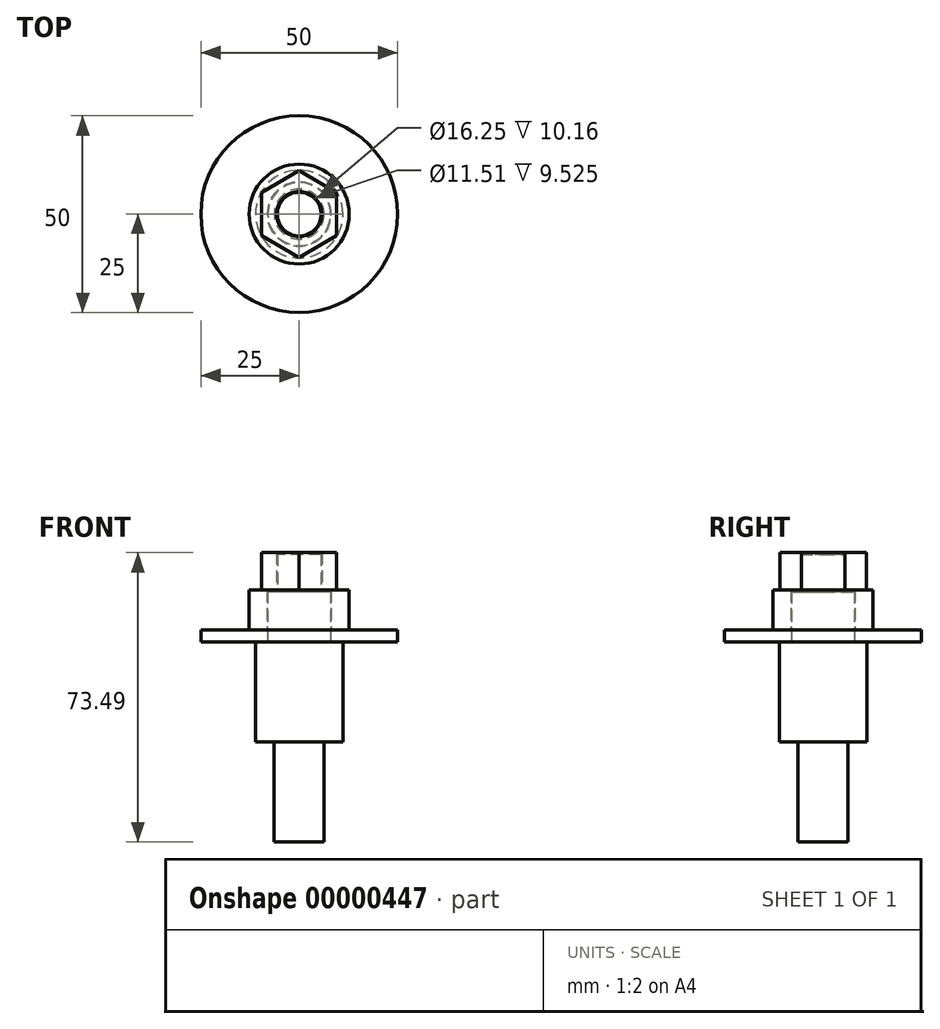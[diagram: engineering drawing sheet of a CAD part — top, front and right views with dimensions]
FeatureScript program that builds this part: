
annotation { "Feature Type Name" : "Feature", "Feature Type Description" : "" }
export const myFeature = defineFeature(function(context is Context, id is Id, definition is map)
    precondition{}
    {
        {
            var Q0;
            Q0=qCreatedBy(makeId("Top.planeOp"),FACE);
            var sketch = newSketch(context, id + "F0", { "sketchPlane" : qUnion([Q0])});
            skCircle(sketch, "E0", {"center": v(0, 0) * mm, "radius": 6.35 * mm});
            skSolve(sketch);
        }
        {
            var Q0;
            Q0 = qSketchRegion(id + "F0", true);
            extrude(context, id + "F1", {"entities" : qUnion([Q0]), "depth" : 25.4 * mm, "offsetDistance" : 25.4 * mm});
        }
        {
            var Q0;
            Q0=makeQuery(id+"F1.opExtrude","CAP_FACE",FACE,{"disambiguationData":[OSD([sQuery(id+"F0.wireOp",EDGE,"E0")])],"isStart":false});
            var sketch = newSketch(context, id + "F2", { "sketchPlane" : qUnion([Q0])});
            skCircle(sketch, "E1", {"center": v(0, 0) * mm, "radius": 11.11 * mm});
            skSolve(sketch);
        }
        {
            var Q0;
            Q0 = qSketchRegion(id + "F2", true);
            extrude(context, id + "F3", {"entities" : qUnion([Q0]), "operationType" : NewBodyOperationType.ADD, "depth" : 25.4 * mm, "offsetDistance" : 25.4 * mm});
        }
        {
            var Q0;
            Q0=makeQuery(id+"F3.opExtrude","CAP_FACE",FACE,{"disambiguationData":[OSD([sQuery(id+"F2.wireOp",EDGE,"E1")])],"isStart":false});
            var sketch = newSketch(context, id + "F4", { "sketchPlane" : qUnion([Q0])});
            skCircle(sketch, "E2", {"center": v(0, 0) * mm, "radius": 8 * mm});
            skSolve(sketch);
        }
        {
            var Q0;
            Q0 = qSketchRegion(id + "F4", true);
            extrude(context, id + "F5", {"entities" : qUnion([Q0]), "operationType" : NewBodyOperationType.ADD, "depth" : 12.7 * mm, "offsetDistance" : 25.4 * mm});
        }
        {
            var Q0;
            Q0=makeQuery(id+"F5.opExtrude","CAP_FACE",FACE,{"disambiguationData":[OSD([sQuery(id+"F4.wireOp",EDGE,"E2")])],"isStart":false});
            var sketch = newSketch(context, id + "F6", { "sketchPlane" : qUnion([Q0])});
            skCircle(sketch, "E3", {"center": v(0, 0) * mm, "radius": 5.55 * mm});
            skSolve(sketch);
        }
        {
            var Q0;
            Q0 = qSketchRegion(id + "F6", true);
            extrude(context, id + "F7", {"entities" : qUnion([Q0]), "operationType" : NewBodyOperationType.ADD, "depth" : 9.52 * mm, "offsetDistance" : 25.4 * mm});
        }
        {
            var Q0;
            Q0=makeQuery(id+"F3.opExtrude","CAP_FACE",FACE,{"disambiguationData":[OSD([sQuery(id+"F2.wireOp",EDGE,"E1")])],"isStart":false});
            var sketch = newSketch(context, id + "F8", { "sketchPlane" : qUnion([Q0])});
            skCircle(sketch, "E4", {"center": v(0, 0) * mm, "radius": 25 * mm});
            skSolve(sketch);
        }
        {
            var Q0;
            Q0 = qSketchRegion(id + "F8", true);
            extrude(context, id + "F9", {"entities" : qUnion([Q0]), "depth" : 3 * mm, "offsetDistance" : 25.4 * mm});
        }
        {
            var Q0;
            Q0=makeQuery(id+"F9.opExtrude","CAP_FACE",FACE,{"disambiguationData":[OSD([sQuery(id+"F8.wireOp",EDGE,"E4")])],"isStart":false});
            var sketch = newSketch(context, id + "F10", { "sketchPlane" : qUnion([Q0])});
            skCircle(sketch, "E5", {"center": v(0, 0) * mm, "radius": 12.7 * mm});
            skCircle(sketch, "E6", {"center": v(0, 0) * mm, "radius": 8.12 * mm});
            skSolve(sketch);
        }
        {
            var Q0;
            Q0 = qSketchRegion(id + "F10", true);
            extrude(context, id + "F11", {"entities" : qUnion([Q0]), "depth" : 10.16 * mm, "offsetDistance" : 25.4 * mm});
        }
        {
            var Q0;
            Q0=makeQuery(id+"F11.opExtrude","CAP_FACE",FACE,{"disambiguationData":[OSD([sQuery(id+"F10.wireOp",EDGE,"E5"),sQuery(id+"F10.wireOp",EDGE,"E6")])],"isStart":false});
            var sketch = newSketch(context, id + "F12", { "sketchPlane" : qUnion([Q0])});
            skCircle(sketch, "E7", {"center": v(0, 0) * mm, "radius": 5.75 * mm});
            skCircle(sketch, "E8.cCircle", {"center": v(0, 0) * mm, "radius": 9.53 * mm, "construction": true});
            skLineSegment(sketch, "E8.0", {"start": v(9.53, 5.5) * mm, "end": v(9.53, -5.5) * mm});
            skLineSegment(sketch, "E8.1", {"start": v(9.53, -5.5) * mm, "end": v(0, -11) * mm});
            skLineSegment(sketch, "E8.2", {"start": v(0, -11) * mm, "end": v(-9.53, -5.5) * mm});
            skLineSegment(sketch, "E8.3", {"start": v(-9.52, -5.5) * mm, "end": v(-9.53, 5.5) * mm});
            skLineSegment(sketch, "E8.4", {"start": v(-9.53, 5.5) * mm, "end": v(0, 11) * mm});
            skLineSegment(sketch, "E8.5", {"start": v(0, 11) * mm, "end": v(9.53, 5.5) * mm});
            skPoint(sketch, "E8.0.midPoint", {"position": v(9.53, 0) * mm});
            skSolve(sketch);
        }
        {
            var Q0;
            Q0 = qSketchRegion(id + "F12", true);
            extrude(context, id + "F13", {"entities" : qUnion([Q0]), "operationType" : NewBodyOperationType.ADD, "depth" : 9.52 * mm, "offsetDistance" : 25.4 * mm});
        }
    });
